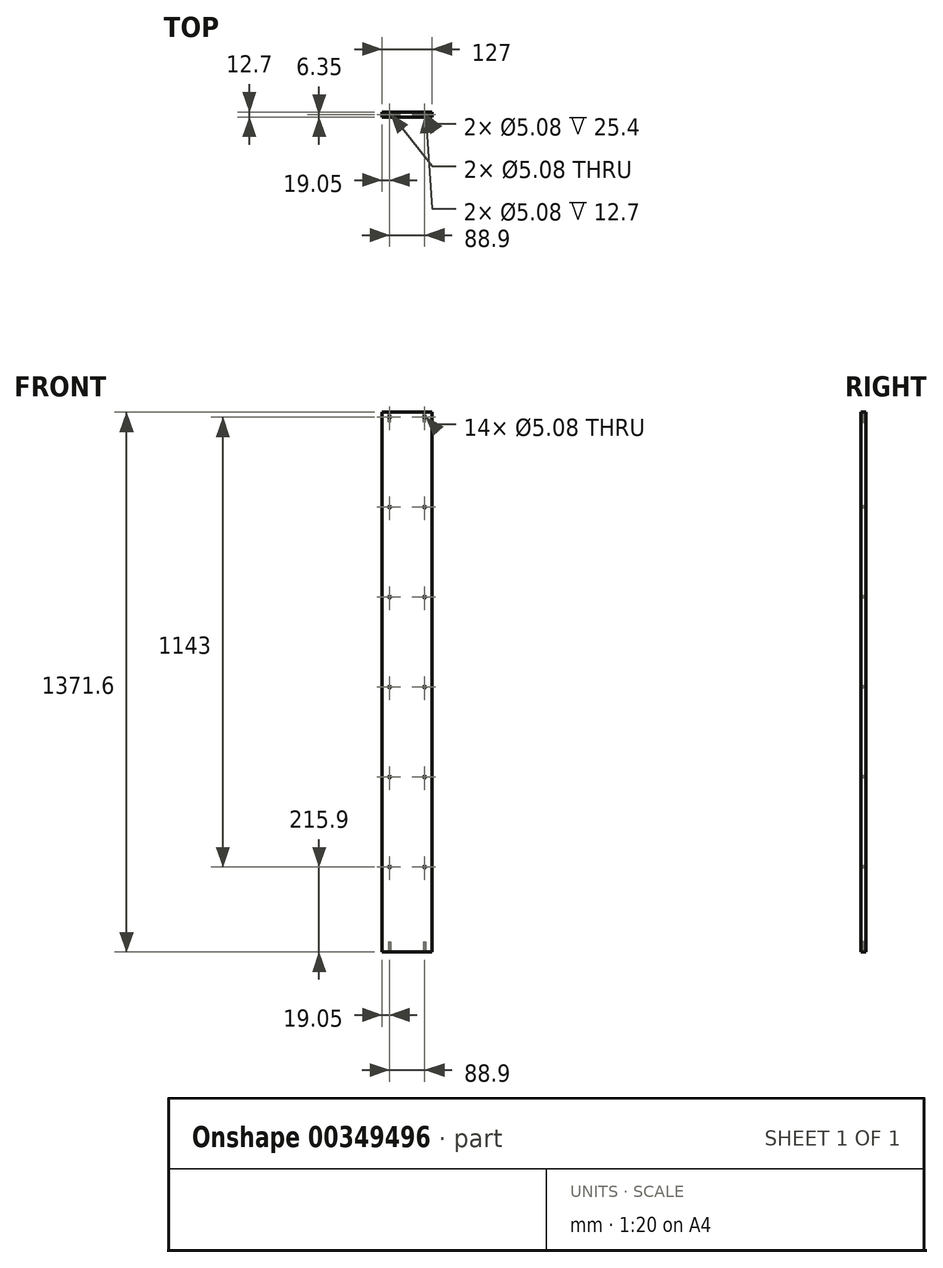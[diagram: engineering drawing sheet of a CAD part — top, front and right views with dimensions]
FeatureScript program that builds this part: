
annotation { "Feature Type Name" : "Feature", "Feature Type Description" : "" }
export const myFeature = defineFeature(function(context is Context, id is Id, definition is map)
    precondition{}
    {
        {
            var Q0;
            Q0=qCreatedBy(makeId("Front.planeOp"),FACE);
            var sketch = newSketch(context, id + "F0", { "sketchPlane" : qUnion([Q0])});
            skLineSegment(sketch, "E0.bottom", {"start": v(-63.5, 685.8) * mm, "end": v(63.5, 685.8) * mm});
            skLineSegment(sketch, "E0.top", {"start": v(-63.5, -685.8) * mm, "end": v(63.5, -685.8) * mm});
            skLineSegment(sketch, "E0.left", {"start": v(-63.5, 685.8) * mm, "end": v(-63.5, -685.8) * mm});
            skLineSegment(sketch, "E0.right", {"start": v(63.5, 685.8) * mm, "end": v(63.5, -685.8) * mm});
            skPoint(sketch, "E1", {"position": v(0, 685.8) * mm});
            skPoint(sketch, "E2", {"position": v(-63.5, 0) * mm});
            skSolve(sketch);
        }
        {
            var Q0;
            Q0 = qSketchRegion(id + "F0", true);
            extrude(context, id + "F1", {"entities" : qUnion([Q0]), "depth" : 12.7 * mm});
        }
        {
            var Q0;
            Q0=makeQuery(id+"F1.opExtrude","CAP_FACE",FACE,{"disambiguationData":[OSD([sQuery(id+"F0.wireOp",EDGE,"E0.bottom"),sQuery(id+"F0.wireOp",EDGE,"E0.top"),sQuery(id+"F0.wireOp",EDGE,"E0.left"),sQuery(id+"F0.wireOp",EDGE,"E0.right")])],"isStart":false});
            var sketch = newSketch(context, id + "F2", { "sketchPlane" : qUnion([Q0])});
            skLineSegment(sketch, "E3", {"start": v(-44.45, 685.8) * mm, "end": v(-44.45, -685.8) * mm, "construction": true});
            skLineSegment(sketch, "E4", {"start": v(44.45, -685.8) * mm, "end": v(44.45, 685.8) * mm, "construction": true});
            skCircle(sketch, "E5", {"center": v(-44.45, -469.9) * mm, "radius": 2.54 * mm});
            skCircle(sketch, "E6", {"center": v(44.45, -469.9) * mm, "radius": 2.54 * mm});
            skCircle(sketch, "E7.0.1.0", {"center": v(44.45, -241.3) * mm, "radius": 2.54 * mm});
            skCircle(sketch, "E7.0.1.1", {"center": v(-44.45, -241.3) * mm, "radius": 2.54 * mm});
            skCircle(sketch, "E7.0.2.0", {"center": v(44.45, -12.7) * mm, "radius": 2.54 * mm});
            skCircle(sketch, "E7.0.2.1", {"center": v(-44.45, -12.7) * mm, "radius": 2.54 * mm});
            skCircle(sketch, "E7.0.3.0", {"center": v(44.45, 215.9) * mm, "radius": 2.54 * mm});
            skCircle(sketch, "E7.0.3.1", {"center": v(-44.45, 215.9) * mm, "radius": 2.54 * mm});
            skCircle(sketch, "E7.0.4.0", {"center": v(44.45, 444.5) * mm, "radius": 2.54 * mm});
            skCircle(sketch, "E7.0.4.1", {"center": v(-44.45, 444.5) * mm, "radius": 2.54 * mm});
            skCircle(sketch, "E7.0.5.0", {"center": v(44.45, 673.1) * mm, "radius": 2.54 * mm});
            skCircle(sketch, "E7.0.5.1", {"center": v(-44.45, 673.1) * mm, "radius": 2.54 * mm});
            skLineSegment(sketch, "E7.direction1", {"start": v(-44.45, -469.9) * mm, "end": v(-19.05, -469.9) * mm, "construction": true});
            skLineSegment(sketch, "E7.direction2", {"start": v(-44.45, -469.9) * mm, "end": v(-44.45, -241.3) * mm, "construction": true});
            skSolve(sketch);
        }
        {
            var Q0;
            Q0 = qSketchRegion(id + "F2", true);
            extrude(context, id + "F3", {"entities" : qUnion([Q0]), "operationType" : NewBodyOperationType.REMOVE, "oppositeDirection" : true, "depth" : 309.88 * mm});
        }
        {
            var Q0;
            Q0=makeQuery(id+"F1.opExtrude","SWEPT_FACE",FACE,{"disambiguationData":[OSD([sQuery(id+"F0.wireOp",EDGE,"E0.top")])]});
            var sketch = newSketch(context, id + "F4", { "sketchPlane" : qUnion([Q0])});
            skLineSegment(sketch, "E8", {"start": v(-63.5, 6.35) * mm, "end": v(63.5, 6.35) * mm, "construction": true});
            skCircle(sketch, "E9", {"center": v(-44.45, 6.35) * mm, "radius": 2.54 * mm});
            skCircle(sketch, "E10", {"center": v(44.45, 6.35) * mm, "radius": 2.54 * mm});
            skSolve(sketch);
        }
        {
            var Q0;
            Q0 = qSketchRegion(id + "F4", true);
            extrude(context, id + "F5", {"entities" : qUnion([Q0]), "operationType" : NewBodyOperationType.REMOVE, "oppositeDirection" : true, "depth" : 25.4 * mm});
        }
        {
            var Q0;
            Q0=makeQuery(id+"F1.opExtrude","SWEPT_FACE",FACE,{"disambiguationData":[OSD([sQuery(id+"F0.wireOp",EDGE,"E0.bottom")])]});
            var sketch = newSketch(context, id + "F6", { "sketchPlane" : qUnion([Q0])});
            skLineSegment(sketch, "E11", {"start": v(-63.5, -6.35) * mm, "end": v(63.5, -6.35) * mm, "construction": true});
            skCircle(sketch, "E12", {"center": v(-44.45, -6.35) * mm, "radius": 2.54 * mm});
            skCircle(sketch, "E13", {"center": v(44.45, -6.35) * mm, "radius": 2.54 * mm});
            skSolve(sketch);
        }
        {
            var Q0;
            Q0 = qSketchRegion(id + "F6", true);
            extrude(context, id + "F7", {"entities" : qUnion([Q0]), "operationType" : NewBodyOperationType.REMOVE, "oppositeDirection" : true, "depth" : 25.4 * mm});
        }
    });
